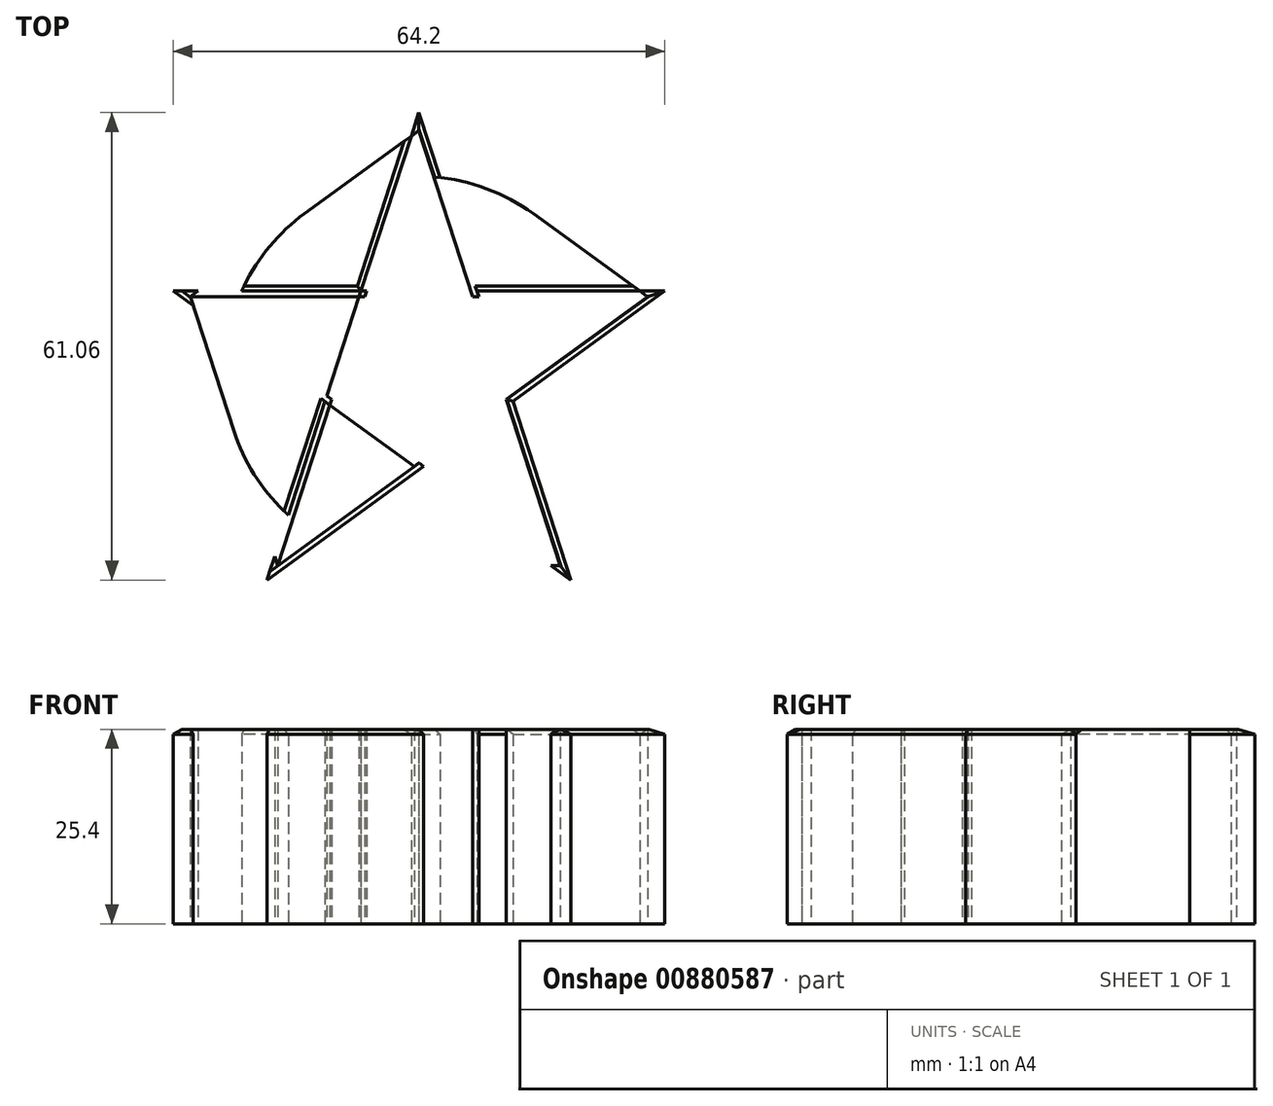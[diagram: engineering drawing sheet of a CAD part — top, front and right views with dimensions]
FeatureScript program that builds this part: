
annotation { "Feature Type Name" : "Feature", "Feature Type Description" : "" }
export const myFeature = defineFeature(function(context is Context, id is Id, definition is map)
    precondition{}
    {
        {
            var Q0;
            Q0=qCreatedBy(makeId("Top.planeOp"),FACE);
            var sketch = newSketch(context, id + "F0", { "sketchPlane" : qUnion([Q0])});
            skCircle(sketch, "E0", {"center": v(0, 0) * mm, "radius": 25.4 * mm});
            skCircle(sketch, "E1.cCircle", {"center": v(0, 0) * mm, "radius": 25.4 * mm, "construction": true});
            skLineSegment(sketch, "E1.0", {"start": v(18.45, -25.4) * mm, "end": v(-18.45, -25.4) * mm});
            skLineSegment(sketch, "E1.1", {"start": v(-18.45, -25.4) * mm, "end": v(-29.86, 9.7) * mm});
            skLineSegment(sketch, "E1.2", {"start": v(-29.86, 9.7) * mm, "end": v(0, 31.4) * mm});
            skLineSegment(sketch, "E1.3", {"start": v(0, 31.4) * mm, "end": v(29.86, 9.7) * mm});
            skLineSegment(sketch, "E1.4", {"start": v(29.86, 9.7) * mm, "end": v(18.45, -25.4) * mm});
            skPoint(sketch, "E1.0.midPoint", {"position": v(0, -25.4) * mm});
            skLineSegment(sketch, "E2", {"start": v(-18.45, -25.4) * mm, "end": v(0, 31.4) * mm});
            skLineSegment(sketch, "E3", {"start": v(0, 31.4) * mm, "end": v(18.45, -25.4) * mm});
            skLineSegment(sketch, "E4", {"start": v(18.45, -25.4) * mm, "end": v(-29.86, 9.7) * mm});
            skLineSegment(sketch, "E5", {"start": v(-29.86, 9.7) * mm, "end": v(29.86, 9.7) * mm});
            skLineSegment(sketch, "E6", {"start": v(29.86, 9.7) * mm, "end": v(-18.45, -25.4) * mm});
            skCircle(sketch, "E7.cCircle", {"center": v(0, 0) * mm, "radius": 27.3 * mm, "construction": true});
            skLineSegment(sketch, "E7.0", {"start": v(19.84, -27.3) * mm, "end": v(-19.84, -27.3) * mm});
            skLineSegment(sketch, "E7.1", {"start": v(-19.84, -27.3) * mm, "end": v(-32.1, 10.43) * mm});
            skLineSegment(sketch, "E7.2", {"start": v(-32.1, 10.43) * mm, "end": v(0, 33.75) * mm});
            skLineSegment(sketch, "E7.3", {"start": v(0, 33.75) * mm, "end": v(32.1, 10.43) * mm});
            skLineSegment(sketch, "E7.4", {"start": v(32.1, 10.43) * mm, "end": v(19.84, -27.3) * mm});
            skPoint(sketch, "E7.0.midPoint", {"position": v(0, -27.3) * mm});
            skLineSegment(sketch, "E8", {"start": v(-19.84, -27.3) * mm, "end": v(0, 33.75) * mm});
            skLineSegment(sketch, "E9", {"start": v(0, 33.75) * mm, "end": v(19.84, -27.3) * mm});
            skLineSegment(sketch, "E10", {"start": v(-32.1, 10.43) * mm, "end": v(32.1, 10.43) * mm});
            skLineSegment(sketch, "E11", {"start": v(32.1, 10.43) * mm, "end": v(-19.84, -27.3) * mm});
            skLineSegment(sketch, "E12", {"start": v(19.84, -27.3) * mm, "end": v(-32.1, 10.43) * mm});
            skSolve(sketch);
        }
        {
            var Q0;
            {var subQ0=sQuery(id+"F0.wireOp",EDGE,"E8");var subQ1=sQuery(id+"F0.wireOp",EDGE,"E0");var subQ2=makeQuery(id+"F0.imprint","INTERSECT",VERTEX,{"disambiguationData":[OD(1.0)],"derivedFrom":[subQ1,subQ0]});Q0=makeQuery(id+"F0.imprint","IMPRINT",FACE,{"disambiguationData":[TD([[makeQuery(id+"F0.imprint","IMPRINT",EDGE,{"disambiguationData":[TD([[subQ2,-1.0]])],"derivedFrom":subQ1}),1.0]])]});}
            var Q1;
            {var subQ0=sQuery(id+"F0.wireOp",EDGE,"E4");var subQ1=sQuery(id+"F0.wireOp",EDGE,"E0");var subQ2=makeQuery(id+"F0.imprint","INTERSECT",VERTEX,{"disambiguationData":[OD(0.0)],"derivedFrom":[subQ1,subQ0]});Q1=makeQuery(id+"F0.imprint","IMPRINT",FACE,{"disambiguationData":[TD([[makeQuery(id+"F0.imprint","IMPRINT",EDGE,{"disambiguationData":[TD([[subQ2,-1.0]])],"derivedFrom":subQ1}),1.0]])]});}
            var Q2;
            {var subQ0=sQuery(id+"F0.wireOp",EDGE,"E6");var subQ1=sQuery(id+"F0.wireOp",EDGE,"E0");var subQ2=makeQuery(id+"F0.imprint","INTERSECT",VERTEX,{"disambiguationData":[OD(1.0)],"derivedFrom":[subQ1,subQ0]});Q2=makeQuery(id+"F0.imprint","IMPRINT",FACE,{"disambiguationData":[TD([[makeQuery(id+"F0.imprint","IMPRINT",EDGE,{"disambiguationData":[TD([[subQ2,-1.0]])],"derivedFrom":subQ1}),1.0]])]});}
            var Q3;
            {var subQ0=sQuery(id+"F0.wireOp",EDGE,"E8");var subQ1=sQuery(id+"F0.wireOp",EDGE,"E0");var subQ2=makeQuery(id+"F0.imprint","INTERSECT",VERTEX,{"disambiguationData":[OD(1.0)],"derivedFrom":[subQ1,subQ0]});Q3=makeQuery(id+"F0.imprint","IMPRINT",FACE,{"disambiguationData":[TD([[makeQuery(id+"F0.imprint","IMPRINT",EDGE,{"disambiguationData":[TD([[subQ2,-1.0]])],"derivedFrom":subQ1}),-1.0]])]});}
            var Q4;
            {var subQ0=sQuery(id+"F0.wireOp",EDGE,"E6");var subQ1=sQuery(id+"F0.wireOp",EDGE,"E0");var subQ2=makeQuery(id+"F0.imprint","INTERSECT",VERTEX,{"disambiguationData":[OD(1.0)],"derivedFrom":[subQ1,subQ0]});Q4=makeQuery(id+"F0.imprint","IMPRINT",FACE,{"disambiguationData":[TD([[makeQuery(id+"F0.imprint","IMPRINT",EDGE,{"disambiguationData":[TD([[subQ2,-1.0]])],"derivedFrom":subQ1}),-1.0]])]});}
            var Q5;
            {var subQ1=sQuery(id+"F0.wireOp",EDGE,"E1.0");var subQ3=sQuery(id+"F0.wireOp",EDGE,"E11");var subQ4=makeQuery(id+"F0.imprint","INTERSECT",VERTEX,{"derivedFrom":[subQ1,subQ3]});Q5=makeQuery(id+"F0.imprint","IMPRINT",FACE,{"disambiguationData":[TD([[makeQuery(id+"F0.imprint","IMPRINT",EDGE,{"disambiguationData":[TD([[subQ4,-1.0]])],"derivedFrom":subQ1}),1.0]])]});}
            var Q6;
            {var subQ0=sQuery(id+"F0.wireOp",EDGE,"E2");var subQ1=sQuery(id+"F0.wireOp",EDGE,"E0");var subQ2=makeQuery(id+"F0.imprint","INTERSECT",VERTEX,{"disambiguationData":[OD(0.0)],"derivedFrom":[subQ1,subQ0]});Q6=makeQuery(id+"F0.imprint","IMPRINT",FACE,{"disambiguationData":[TD([[makeQuery(id+"F0.imprint","IMPRINT",EDGE,{"disambiguationData":[TD([[subQ2,-1.0]])],"derivedFrom":subQ1}),1.0]])]});}
            var Q7;
            {var subQ0=sQuery(id+"F0.wireOp",EDGE,"E9");var subQ1=sQuery(id+"F0.wireOp",EDGE,"E0");var subQ2=makeQuery(id+"F0.imprint","INTERSECT",VERTEX,{"disambiguationData":[OD(0.0)],"derivedFrom":[subQ1,subQ0]});Q7=makeQuery(id+"F0.imprint","IMPRINT",FACE,{"disambiguationData":[TD([[makeQuery(id+"F0.imprint","IMPRINT",EDGE,{"disambiguationData":[TD([[subQ2,-1.0]])],"derivedFrom":subQ1}),1.0]])]});}
            var Q8;
            {var subQ0=sQuery(id+"F0.wireOp",EDGE,"E6");var subQ1=sQuery(id+"F0.wireOp",EDGE,"E0");var subQ2=makeQuery(id+"F0.imprint","INTERSECT",VERTEX,{"disambiguationData":[OD(0.0)],"derivedFrom":[subQ1,subQ0]});Q8=makeQuery(id+"F0.imprint","IMPRINT",FACE,{"disambiguationData":[TD([[makeQuery(id+"F0.imprint","IMPRINT",EDGE,{"disambiguationData":[TD([[subQ2,1.0]])],"derivedFrom":subQ1}),1.0]])]});}
            var Q9;
            {var subQ0=sQuery(id+"F0.wireOp",EDGE,"E3");var subQ1=sQuery(id+"F0.wireOp",EDGE,"E0");var subQ2=makeQuery(id+"F0.imprint","INTERSECT",VERTEX,{"disambiguationData":[OD(1.0)],"derivedFrom":[subQ1,subQ0]});Q9=makeQuery(id+"F0.imprint","IMPRINT",FACE,{"disambiguationData":[TD([[makeQuery(id+"F0.imprint","IMPRINT",EDGE,{"disambiguationData":[TD([[subQ2,-1.0]])],"derivedFrom":subQ1}),1.0]])]});}
            var Q10;
            {var subQ0=sQuery(id+"F0.wireOp",EDGE,"E6");var subQ1=sQuery(id+"F0.wireOp",EDGE,"E3");var subQ2=makeQuery(id+"F0.imprint","INTERSECT",VERTEX,{"derivedFrom":[subQ1,subQ0]});Q10=makeQuery(id+"F0.imprint","IMPRINT",FACE,{"disambiguationData":[TD([[makeQuery(id+"F0.imprint","IMPRINT",EDGE,{"disambiguationData":[TD([[subQ2,-1.0]])],"derivedFrom":subQ1}),1.0]])]});}
            var Q11;
            {var subQ0=sQuery(id+"F0.wireOp",EDGE,"E6");var subQ1=sQuery(id+"F0.wireOp",EDGE,"E0");var subQ2=makeQuery(id+"F0.imprint","INTERSECT",VERTEX,{"disambiguationData":[OD(0.0)],"derivedFrom":[subQ1,subQ0]});Q11=makeQuery(id+"F0.imprint","IMPRINT",FACE,{"disambiguationData":[TD([[makeQuery(id+"F0.imprint","IMPRINT",EDGE,{"disambiguationData":[TD([[subQ2,1.0]])],"derivedFrom":subQ1}),-1.0]])]});}
            var Q12;
            {var subQ1=sQuery(id+"F0.wireOp",EDGE,"E1.3");var subQ3=sQuery(id+"F0.wireOp",EDGE,"E10");var subQ4=makeQuery(id+"F0.imprint","INTERSECT",VERTEX,{"derivedFrom":[subQ1,subQ3]});Q12=makeQuery(id+"F0.imprint","IMPRINT",FACE,{"disambiguationData":[TD([[makeQuery(id+"F0.imprint","IMPRINT",EDGE,{"disambiguationData":[TD([[subQ4,-1.0]])],"derivedFrom":subQ1}),1.0]])]});}
            var Q13;
            {var subQ0=sQuery(id+"F0.wireOp",EDGE,"E5");var subQ1=sQuery(id+"F0.wireOp",EDGE,"E0");var subQ2=makeQuery(id+"F0.imprint","INTERSECT",VERTEX,{"disambiguationData":[OD(0.0)],"derivedFrom":[subQ1,subQ0]});Q13=makeQuery(id+"F0.imprint","IMPRINT",FACE,{"disambiguationData":[TD([[makeQuery(id+"F0.imprint","IMPRINT",EDGE,{"disambiguationData":[TD([[subQ2,-1.0]])],"derivedFrom":subQ1}),-1.0]])]});}
            var Q14;
            {var subQ0=sQuery(id+"F0.wireOp",EDGE,"E5");var subQ1=sQuery(id+"F0.wireOp",EDGE,"E0");var subQ2=makeQuery(id+"F0.imprint","INTERSECT",VERTEX,{"disambiguationData":[OD(0.0)],"derivedFrom":[subQ1,subQ0]});Q14=makeQuery(id+"F0.imprint","IMPRINT",FACE,{"disambiguationData":[TD([[makeQuery(id+"F0.imprint","IMPRINT",EDGE,{"disambiguationData":[TD([[subQ2,-1.0]])],"derivedFrom":subQ1}),1.0]])]});}
            var Q15;
            {var subQ0=sQuery(id+"F0.wireOp",EDGE,"E10");var subQ1=sQuery(id+"F0.wireOp",EDGE,"E3");var subQ2=makeQuery(id+"F0.imprint","INTERSECT",VERTEX,{"derivedFrom":[subQ1,subQ0]});Q15=makeQuery(id+"F0.imprint","IMPRINT",FACE,{"disambiguationData":[TD([[makeQuery(id+"F0.imprint","IMPRINT",EDGE,{"disambiguationData":[TD([[subQ2,-1.0]])],"derivedFrom":subQ1}),1.0]])]});}
            var Q16;
            {var subQ0=sQuery(id+"F0.wireOp",EDGE,"E10");var subQ1=sQuery(id+"F0.wireOp",EDGE,"E0");var subQ2=makeQuery(id+"F0.imprint","INTERSECT",VERTEX,{"disambiguationData":[OD(1.0)],"derivedFrom":[subQ1,subQ0]});Q16=makeQuery(id+"F0.imprint","IMPRINT",FACE,{"disambiguationData":[TD([[makeQuery(id+"F0.imprint","IMPRINT",EDGE,{"disambiguationData":[TD([[subQ2,-1.0]])],"derivedFrom":subQ1}),1.0]])]});}
            var Q17;
            {var subQ0=sQuery(id+"F0.wireOp",EDGE,"E10");var subQ1=sQuery(id+"F0.wireOp",EDGE,"E0");var subQ2=makeQuery(id+"F0.imprint","INTERSECT",VERTEX,{"disambiguationData":[OD(1.0)],"derivedFrom":[subQ1,subQ0]});Q17=makeQuery(id+"F0.imprint","IMPRINT",FACE,{"disambiguationData":[TD([[makeQuery(id+"F0.imprint","IMPRINT",EDGE,{"disambiguationData":[TD([[subQ2,-1.0]])],"derivedFrom":subQ1}),-1.0]])]});}
            var Q18;
            {var subQ1=sQuery(id+"F0.wireOp",EDGE,"E1.1");var subQ3=sQuery(id+"F0.wireOp",EDGE,"E12");var subQ4=makeQuery(id+"F0.imprint","INTERSECT",VERTEX,{"derivedFrom":[subQ1,subQ3]});Q18=makeQuery(id+"F0.imprint","IMPRINT",FACE,{"disambiguationData":[TD([[makeQuery(id+"F0.imprint","IMPRINT",EDGE,{"disambiguationData":[TD([[subQ4,-1.0]])],"derivedFrom":subQ1}),1.0]])]});}
            var Q19;
            {var subQ0=sQuery(id+"F0.wireOp",EDGE,"E4");var subQ1=sQuery(id+"F0.wireOp",EDGE,"E0");var subQ2=makeQuery(id+"F0.imprint","INTERSECT",VERTEX,{"disambiguationData":[OD(0.0)],"derivedFrom":[subQ1,subQ0]});Q19=makeQuery(id+"F0.imprint","IMPRINT",FACE,{"disambiguationData":[TD([[makeQuery(id+"F0.imprint","IMPRINT",EDGE,{"disambiguationData":[TD([[subQ2,-1.0]])],"derivedFrom":subQ1}),-1.0]])]});}
            var Q20;
            {var subQ0=sQuery(id+"F0.wireOp",EDGE,"E5");var subQ1=sQuery(id+"F0.wireOp",EDGE,"E2");var subQ2=makeQuery(id+"F0.imprint","INTERSECT",VERTEX,{"derivedFrom":[subQ1,subQ0]});Q20=makeQuery(id+"F0.imprint","IMPRINT",FACE,{"disambiguationData":[TD([[makeQuery(id+"F0.imprint","IMPRINT",EDGE,{"disambiguationData":[TD([[subQ2,-1.0]])],"derivedFrom":subQ1}),1.0]])]});}
            var Q21;
            {var subQ0=sQuery(id+"F0.wireOp",EDGE,"E11");var subQ1=sQuery(id+"F0.wireOp",EDGE,"E4");var subQ2=makeQuery(id+"F0.imprint","INTERSECT",VERTEX,{"derivedFrom":[subQ1,subQ0]});Q21=makeQuery(id+"F0.imprint","IMPRINT",FACE,{"disambiguationData":[TD([[makeQuery(id+"F0.imprint","IMPRINT",EDGE,{"disambiguationData":[TD([[subQ2,-1.0]])],"derivedFrom":subQ1}),1.0]])]});}
            var Q22;
            {var subQ0=sQuery(id+"F0.wireOp",EDGE,"E12");var subQ1=sQuery(id+"F0.wireOp",EDGE,"E0");var subQ2=makeQuery(id+"F0.imprint","INTERSECT",VERTEX,{"disambiguationData":[OD(1.0)],"derivedFrom":[subQ1,subQ0]});Q22=makeQuery(id+"F0.imprint","IMPRINT",FACE,{"disambiguationData":[TD([[makeQuery(id+"F0.imprint","IMPRINT",EDGE,{"disambiguationData":[TD([[subQ2,-1.0]])],"derivedFrom":subQ1}),1.0]])]});}
            var Q23;
            {var subQ0=sQuery(id+"F0.wireOp",EDGE,"E12");var subQ1=sQuery(id+"F0.wireOp",EDGE,"E0");var subQ2=makeQuery(id+"F0.imprint","INTERSECT",VERTEX,{"disambiguationData":[OD(1.0)],"derivedFrom":[subQ1,subQ0]});Q23=makeQuery(id+"F0.imprint","IMPRINT",FACE,{"disambiguationData":[TD([[makeQuery(id+"F0.imprint","IMPRINT",EDGE,{"disambiguationData":[TD([[subQ2,-1.0]])],"derivedFrom":subQ1}),-1.0]])]});}
            var Q24;
            {var subQ0=sQuery(id+"F0.wireOp",EDGE,"E3");var subQ1=sQuery(id+"F0.wireOp",EDGE,"E0");var subQ2=makeQuery(id+"F0.imprint","INTERSECT",VERTEX,{"disambiguationData":[OD(1.0)],"derivedFrom":[subQ1,subQ0]});Q24=makeQuery(id+"F0.imprint","IMPRINT",FACE,{"disambiguationData":[TD([[makeQuery(id+"F0.imprint","IMPRINT",EDGE,{"disambiguationData":[TD([[subQ2,-1.0]])],"derivedFrom":subQ1}),-1.0]])]});}
            var Q25;
            {var subQ1=sQuery(id+"F0.wireOp",EDGE,"E1.0");var subQ3=sQuery(id+"F0.wireOp",EDGE,"E12");var subQ4=makeQuery(id+"F0.imprint","INTERSECT",VERTEX,{"derivedFrom":[subQ1,subQ3]});Q25=makeQuery(id+"F0.imprint","IMPRINT",FACE,{"disambiguationData":[TD([[makeQuery(id+"F0.imprint","IMPRINT",EDGE,{"disambiguationData":[TD([[subQ4,1.0]])],"derivedFrom":subQ1}),1.0]])]});}
            var Q26;
            {var subQ0=sQuery(id+"F0.wireOp",EDGE,"E2");var subQ1=sQuery(id+"F0.wireOp",EDGE,"E0");var subQ2=makeQuery(id+"F0.imprint","INTERSECT",VERTEX,{"disambiguationData":[OD(0.0)],"derivedFrom":[subQ1,subQ0]});Q26=makeQuery(id+"F0.imprint","IMPRINT",FACE,{"disambiguationData":[TD([[makeQuery(id+"F0.imprint","IMPRINT",EDGE,{"disambiguationData":[TD([[subQ2,-1.0]])],"derivedFrom":subQ1}),-1.0]])]});}
            var Q27;
            {var subQ0=sQuery(id+"F0.wireOp",EDGE,"E9");var subQ1=sQuery(id+"F0.wireOp",EDGE,"E0");var subQ2=makeQuery(id+"F0.imprint","INTERSECT",VERTEX,{"disambiguationData":[OD(0.0)],"derivedFrom":[subQ1,subQ0]});Q27=makeQuery(id+"F0.imprint","IMPRINT",FACE,{"disambiguationData":[TD([[makeQuery(id+"F0.imprint","IMPRINT",EDGE,{"disambiguationData":[TD([[subQ2,-1.0]])],"derivedFrom":subQ1}),-1.0]])]});}
            var Q28;
            {var subQ1=sQuery(id+"F0.wireOp",EDGE,"E1.2");var subQ3=sQuery(id+"F0.wireOp",EDGE,"E8");var subQ4=makeQuery(id+"F0.imprint","INTERSECT",VERTEX,{"derivedFrom":[subQ1,subQ3]});Q28=makeQuery(id+"F0.imprint","IMPRINT",FACE,{"disambiguationData":[TD([[makeQuery(id+"F0.imprint","IMPRINT",EDGE,{"disambiguationData":[TD([[subQ4,-1.0]])],"derivedFrom":subQ1}),1.0]])]});}
            var Q29;
            {var subQ0=sQuery(id+"F0.wireOp",EDGE,"E12");var subQ1=sQuery(id+"F0.wireOp",EDGE,"E2");var subQ2=makeQuery(id+"F0.imprint","INTERSECT",VERTEX,{"derivedFrom":[subQ1,subQ0]});Q29=makeQuery(id+"F0.imprint","IMPRINT",FACE,{"disambiguationData":[TD([[makeQuery(id+"F0.imprint","IMPRINT",EDGE,{"disambiguationData":[TD([[subQ2,-1.0]])],"derivedFrom":subQ1}),1.0]])]});}
            extrude(context, id + "F1", {"entities" : qUnion([Q0, Q1, Q2, Q3, Q4, Q5, Q6, Q7, Q8, Q9, Q10, Q11, Q12, Q13, Q14, Q15, Q16, Q17, Q18, Q19, Q20, Q21, Q22, Q23, Q24, Q25, Q26, Q27, Q28, Q29]), "depth" : 25.4 * mm, "offsetDistance" : 25.4 * mm});
        }
        {
            var Q0;
            {var subQ0=sQuery(id+"F0.wireOp",EDGE,"E10");var subQ1=makeQuery(id+"F0.imprint","INTERSECT",VERTEX,{"disambiguationData":[OD(1.0)],"derivedFrom":[sQuery(id+"F0.wireOp",EDGE,"E0"),subQ0]});var subQ2=makeQuery(id+"F0.imprint","INTERSECT",VERTEX,{"derivedFrom":[sQuery(id+"F0.wireOp",EDGE,"E1.2"),subQ0]});Q0=makeQuery(id+"F1.opExtrude","CAP_EDGE",EDGE,{"disambiguationData":[OSD([subQ0]),TDD([makeQuery(id+"F0.imprint","IMPRINT",EDGE,{"disambiguationData":[TD([[subQ2,1.0]])],"derivedFrom":subQ0}),makeQuery(id+"F0.imprint","IMPRINT",EDGE,{"disambiguationData":[TD([[subQ1,1.0]])],"derivedFrom":subQ0}),makeQuery(id+"F0.imprint","IMPRINT",EDGE,{"disambiguationData":[TD([[subQ1,-1.0]])],"derivedFrom":subQ0})])],"isStart":false});}
            var Q1;
            {var subQ0=sQuery(id+"F0.wireOp",EDGE,"E12");var subQ1=makeQuery(id+"F0.imprint","INTERSECT",VERTEX,{"derivedFrom":[sQuery(id+"F0.wireOp",EDGE,"E1.1"),subQ0]});var subQ2=makeQuery(id+"F0.imprint","INTERSECT",VERTEX,{"disambiguationData":[OD(0.0)],"derivedFrom":[sQuery(id+"F0.wireOp",EDGE,"E0"),subQ0]});Q1=makeQuery(id+"F1.opExtrude","CAP_EDGE",EDGE,{"disambiguationData":[OSD([subQ0]),TDD([makeQuery(id+"F0.imprint","IMPRINT",EDGE,{"disambiguationData":[TD([[subQ2,1.0]])],"derivedFrom":subQ0}),makeQuery(id+"F0.imprint","IMPRINT",EDGE,{"disambiguationData":[TD([[subQ2,-1.0]])],"derivedFrom":subQ0}),makeQuery(id+"F0.imprint","IMPRINT",EDGE,{"disambiguationData":[TD([[subQ1,-1.0]])],"derivedFrom":subQ0})])],"isStart":false});}
            var Q2;
            {var subQ0=sQuery(id+"F0.wireOp",EDGE,"E8");var subQ1=makeQuery(id+"F0.imprint","INTERSECT",VERTEX,{"disambiguationData":[OD(1.0)],"derivedFrom":[sQuery(id+"F0.wireOp",EDGE,"E0"),subQ0]});var subQ2=makeQuery(id+"F0.imprint","INTERSECT",VERTEX,{"derivedFrom":[sQuery(id+"F0.wireOp",EDGE,"E1.1"),subQ0]});Q2=makeQuery(id+"F1.opExtrude","CAP_EDGE",EDGE,{"disambiguationData":[OSD([subQ0]),TDD([makeQuery(id+"F0.imprint","IMPRINT",EDGE,{"disambiguationData":[TD([[subQ2,1.0]])],"derivedFrom":subQ0}),makeQuery(id+"F0.imprint","IMPRINT",EDGE,{"disambiguationData":[TD([[subQ1,1.0]])],"derivedFrom":subQ0}),makeQuery(id+"F0.imprint","IMPRINT",EDGE,{"disambiguationData":[TD([[subQ1,-1.0]])],"derivedFrom":subQ0})])],"isStart":false});}
            var Q3;
            {var subQ0=sQuery(id+"F0.wireOp",EDGE,"E11");var subQ1=makeQuery(id+"F0.imprint","INTERSECT",VERTEX,{"derivedFrom":[sQuery(id+"F0.wireOp",EDGE,"E1.0"),subQ0]});var subQ2=makeQuery(id+"F0.imprint","INTERSECT",VERTEX,{"disambiguationData":[OD(1.0)],"derivedFrom":[sQuery(id+"F0.wireOp",EDGE,"E0"),subQ0]});Q3=makeQuery(id+"F1.opExtrude","CAP_EDGE",EDGE,{"disambiguationData":[OSD([subQ0]),TDD([makeQuery(id+"F0.imprint","IMPRINT",EDGE,{"disambiguationData":[TD([[subQ2,1.0]])],"derivedFrom":subQ0}),makeQuery(id+"F0.imprint","IMPRINT",EDGE,{"disambiguationData":[TD([[subQ2,-1.0]])],"derivedFrom":subQ0}),makeQuery(id+"F0.imprint","IMPRINT",EDGE,{"disambiguationData":[TD([[subQ1,-1.0]])],"derivedFrom":subQ0})])],"isStart":false});}
            var Q4;
            {var subQ0=sQuery(id+"F0.wireOp",EDGE,"E12");var subQ1=makeQuery(id+"F0.imprint","INTERSECT",VERTEX,{"disambiguationData":[OD(1.0)],"derivedFrom":[sQuery(id+"F0.wireOp",EDGE,"E0"),subQ0]});var subQ2=makeQuery(id+"F0.imprint","INTERSECT",VERTEX,{"derivedFrom":[sQuery(id+"F0.wireOp",EDGE,"E1.0"),subQ0]});Q4=makeQuery(id+"F1.opExtrude","CAP_EDGE",EDGE,{"disambiguationData":[OSD([subQ0]),TDD([makeQuery(id+"F0.imprint","IMPRINT",EDGE,{"disambiguationData":[TD([[subQ2,1.0]])],"derivedFrom":subQ0}),makeQuery(id+"F0.imprint","IMPRINT",EDGE,{"disambiguationData":[TD([[subQ1,1.0]])],"derivedFrom":subQ0}),makeQuery(id+"F0.imprint","IMPRINT",EDGE,{"disambiguationData":[TD([[subQ1,-1.0]])],"derivedFrom":subQ0})])],"isStart":false});}
            var Q5;
            {var subQ0=sQuery(id+"F0.wireOp",EDGE,"E9");var subQ1=makeQuery(id+"F0.imprint","INTERSECT",VERTEX,{"derivedFrom":[sQuery(id+"F0.wireOp",EDGE,"E1.4"),subQ0]});var subQ2=makeQuery(id+"F0.imprint","INTERSECT",VERTEX,{"disambiguationData":[OD(1.0)],"derivedFrom":[sQuery(id+"F0.wireOp",EDGE,"E0"),subQ0]});Q5=makeQuery(id+"F1.opExtrude","CAP_EDGE",EDGE,{"disambiguationData":[OSD([subQ0]),TDD([makeQuery(id+"F0.imprint","IMPRINT",EDGE,{"disambiguationData":[TD([[subQ2,1.0]])],"derivedFrom":subQ0}),makeQuery(id+"F0.imprint","IMPRINT",EDGE,{"disambiguationData":[TD([[subQ2,-1.0]])],"derivedFrom":subQ0}),makeQuery(id+"F0.imprint","IMPRINT",EDGE,{"disambiguationData":[TD([[subQ1,-1.0]])],"derivedFrom":subQ0})])],"isStart":false});}
            var Q6;
            {var subQ0=sQuery(id+"F0.wireOp",EDGE,"E11");var subQ1=makeQuery(id+"F0.imprint","INTERSECT",VERTEX,{"disambiguationData":[OD(0.0)],"derivedFrom":[sQuery(id+"F0.wireOp",EDGE,"E0"),subQ0]});var subQ2=makeQuery(id+"F0.imprint","INTERSECT",VERTEX,{"derivedFrom":[sQuery(id+"F0.wireOp",EDGE,"E1.4"),subQ0]});Q6=makeQuery(id+"F1.opExtrude","CAP_EDGE",EDGE,{"disambiguationData":[OSD([subQ0]),TDD([makeQuery(id+"F0.imprint","IMPRINT",EDGE,{"disambiguationData":[TD([[subQ2,1.0]])],"derivedFrom":subQ0}),makeQuery(id+"F0.imprint","IMPRINT",EDGE,{"disambiguationData":[TD([[subQ1,1.0]])],"derivedFrom":subQ0}),makeQuery(id+"F0.imprint","IMPRINT",EDGE,{"disambiguationData":[TD([[subQ1,-1.0]])],"derivedFrom":subQ0})])],"isStart":false});}
            var Q7;
            {var subQ0=sQuery(id+"F0.wireOp",EDGE,"E10");var subQ1=makeQuery(id+"F0.imprint","INTERSECT",VERTEX,{"derivedFrom":[sQuery(id+"F0.wireOp",EDGE,"E1.3"),subQ0]});var subQ2=makeQuery(id+"F0.imprint","INTERSECT",VERTEX,{"disambiguationData":[OD(0.0)],"derivedFrom":[sQuery(id+"F0.wireOp",EDGE,"E0"),subQ0]});Q7=makeQuery(id+"F1.opExtrude","CAP_EDGE",EDGE,{"disambiguationData":[OSD([subQ0]),TDD([makeQuery(id+"F0.imprint","IMPRINT",EDGE,{"disambiguationData":[TD([[subQ2,1.0]])],"derivedFrom":subQ0}),makeQuery(id+"F0.imprint","IMPRINT",EDGE,{"disambiguationData":[TD([[subQ2,-1.0]])],"derivedFrom":subQ0}),makeQuery(id+"F0.imprint","IMPRINT",EDGE,{"disambiguationData":[TD([[subQ1,-1.0]])],"derivedFrom":subQ0})])],"isStart":false});}
            var Q8;
            {var subQ0=sQuery(id+"F0.wireOp",EDGE,"E9");var subQ1=makeQuery(id+"F0.imprint","INTERSECT",VERTEX,{"disambiguationData":[OD(0.0)],"derivedFrom":[sQuery(id+"F0.wireOp",EDGE,"E0"),subQ0]});var subQ2=makeQuery(id+"F0.imprint","INTERSECT",VERTEX,{"derivedFrom":[sQuery(id+"F0.wireOp",EDGE,"E1.3"),subQ0]});Q8=makeQuery(id+"F1.opExtrude","CAP_EDGE",EDGE,{"disambiguationData":[OSD([subQ0]),TDD([makeQuery(id+"F0.imprint","IMPRINT",EDGE,{"disambiguationData":[TD([[subQ2,1.0]])],"derivedFrom":subQ0}),makeQuery(id+"F0.imprint","IMPRINT",EDGE,{"disambiguationData":[TD([[subQ1,1.0]])],"derivedFrom":subQ0}),makeQuery(id+"F0.imprint","IMPRINT",EDGE,{"disambiguationData":[TD([[subQ1,-1.0]])],"derivedFrom":subQ0})])],"isStart":false});}
            var Q9;
            {var subQ0=sQuery(id+"F0.wireOp",EDGE,"E8");var subQ1=makeQuery(id+"F0.imprint","INTERSECT",VERTEX,{"derivedFrom":[sQuery(id+"F0.wireOp",EDGE,"E1.2"),subQ0]});var subQ2=makeQuery(id+"F0.imprint","INTERSECT",VERTEX,{"disambiguationData":[OD(0.0)],"derivedFrom":[sQuery(id+"F0.wireOp",EDGE,"E0"),subQ0]});Q9=makeQuery(id+"F1.opExtrude","CAP_EDGE",EDGE,{"disambiguationData":[OSD([subQ0]),TDD([makeQuery(id+"F0.imprint","IMPRINT",EDGE,{"disambiguationData":[TD([[subQ2,1.0]])],"derivedFrom":subQ0}),makeQuery(id+"F0.imprint","IMPRINT",EDGE,{"disambiguationData":[TD([[subQ2,-1.0]])],"derivedFrom":subQ0}),makeQuery(id+"F0.imprint","IMPRINT",EDGE,{"disambiguationData":[TD([[subQ1,-1.0]])],"derivedFrom":subQ0})])],"isStart":false});}
            chamfer(context, id + "F2", {"entities" : qUnion([Q0, Q1, Q2, Q3, Q4, Q5, Q6, Q7, Q8, Q9]), "width" : 0.66 * mm, "tangentPropagation" : true});
        }
    });
